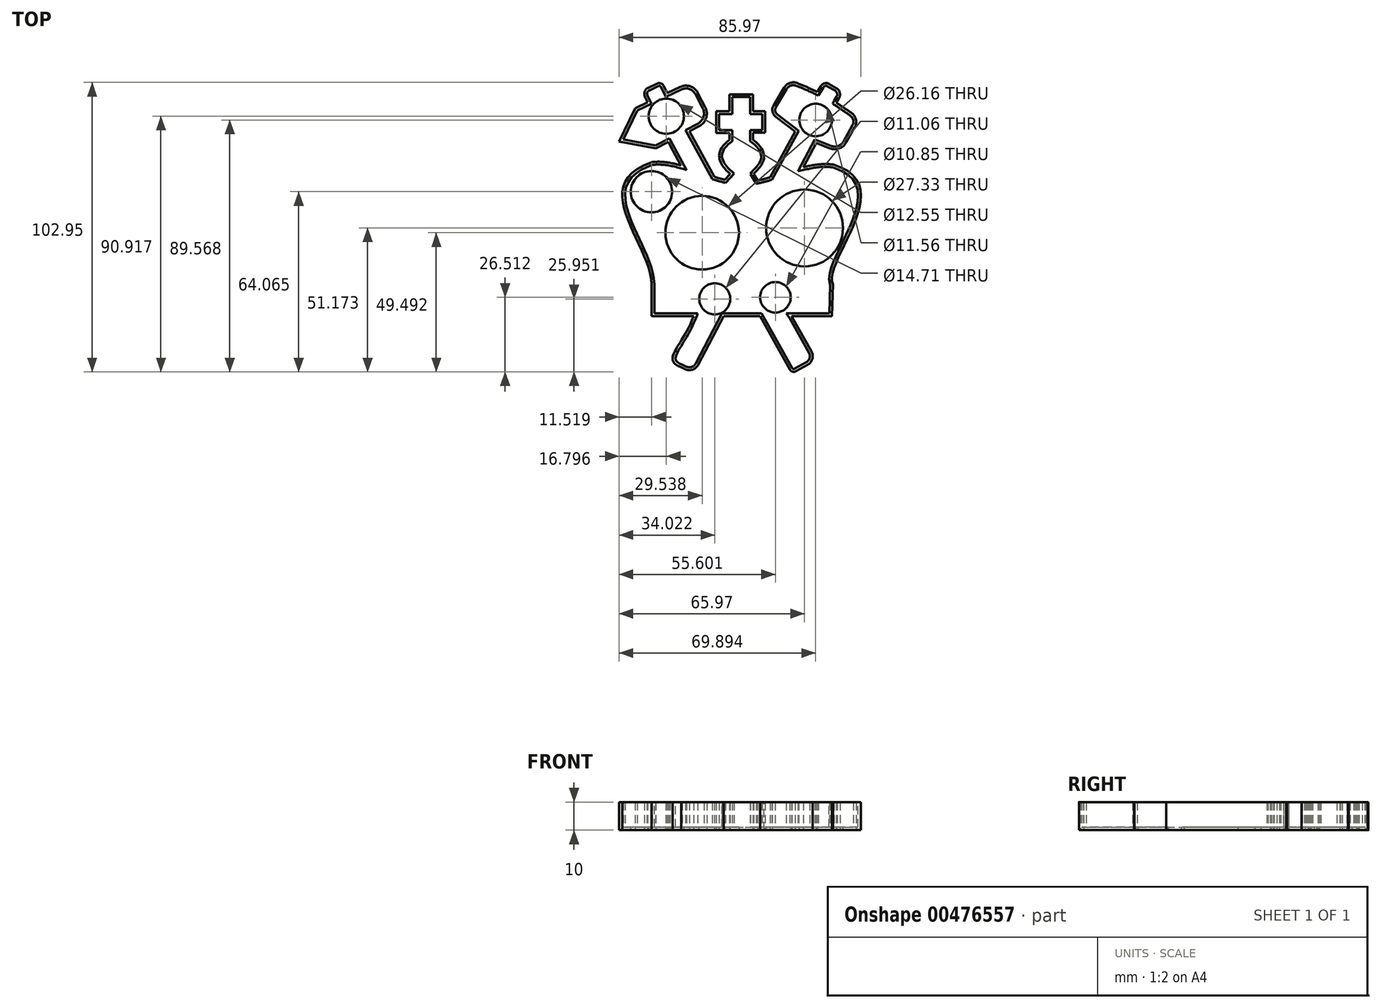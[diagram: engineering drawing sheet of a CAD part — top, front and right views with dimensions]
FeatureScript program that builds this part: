
annotation { "Feature Type Name" : "Feature", "Feature Type Description" : "" }
export const myFeature = defineFeature(function(context is Context, id is Id, definition is map)
    precondition{}
    {
        {
            var Q0;
            Q0=qCreatedBy(makeId("Top.planeOp"),FACE);
            var sketch = newSketch(context, id + "F0", { "sketchPlane" : qUnion([Q0])});
            skLineSegment(sketch, "E0", {"start": v(-31.75, -27.45) * mm, "end": v(32.44, -27.45) * mm});
            skLineSegment(sketch, "E1", {"start": v(-31.75, -27.45) * mm, "end": v(-31.75, -16.16) * mm});
            skLineSegment(sketch, "E2", {"start": v(-31.75, -16.16) * mm, "end": v(32.84, -16.16) * mm});
            skLineSegment(sketch, "E3", {"start": v(32.84, -16.16) * mm, "end": v(32.44, -27.45) * mm});
            skFitSpline(sketch, "E4", {"points": [v(-16.76, -27.45) * mm, v(-21.2, -45.6) * mm], "startDerivative": vector(-12.7, -33.27) * mm, "endDerivative": vector(21.77, -7.86) * mm});
            skLineSegment(sketch, "E5", {"start": v(-21.2, -45.6) * mm, "end": v(-19.95, -46.24) * mm});
            skLineSegment(sketch, "E6", {"start": v(-15.02, -44.65) * mm, "end": v(-6.11, -27.45) * mm});
            skPoint(sketch, "E7.visualSharp", {"position": v(-16.7, -47.89) * mm});
            skArc(sketch, "E7.filletArc", {"start": v(-19.95, -46.24) * mm, "mid": v(-17.16, -46.46) * mm, "end": v(-15.02, -44.65) * mm});
            skLineSegment(sketch, "E8", {"start": v(6.83, -27.45) * mm, "end": v(17.44, -46.43) * mm});
            skLineSegment(sketch, "E9", {"start": v(19.63, -47.05) * mm, "end": v(23.82, -44.7) * mm});
            skLineSegment(sketch, "E10", {"start": v(25.14, -40.03) * mm, "end": v(18.22, -27.65) * mm});
            skPoint(sketch, "E11.visualSharp", {"position": v(18.22, -47.84) * mm});
            skArc(sketch, "E11.filletArc", {"start": v(17.44, -46.43) * mm, "mid": v(18.4, -47.2) * mm, "end": v(19.63, -47.05) * mm});
            skPoint(sketch, "E12.visualSharp", {"position": v(26.82, -43.03) * mm});
            skArc(sketch, "E12.filletArc", {"start": v(23.82, -44.7) * mm, "mid": v(25.45, -42.64) * mm, "end": v(25.14, -40.03) * mm});
            skFitSpline(sketch, "E13", {"points": [v(32.84, -16.16) * mm, v(32.84, 26.48) * mm], "startDerivative": vector(-12.24, 24.57) * mm, "endDerivative": vector(-72.32, 21.35) * mm});
            skFitSpline(sketch, "E14", {"points": [v(-31.75, -16.16) * mm, v(-31.75, 27.32) * mm], "startDerivative": vector(0, 42.93) * mm, "endDerivative": vector(70.07, 24.77) * mm});
            skFitSpline(sketch, "E15", {"points": [v(-31.75, 27.32) * mm, v(-5.7, 21.06) * mm], "startDerivative": vector(25.6, 3.42) * mm, "endDerivative": vector(26.19, -6.26) * mm});
            skFitSpline(sketch, "E16", {"points": [v(32.84, 26.48) * mm, v(5.98, 20.79) * mm], "startDerivative": vector(-26.76, 3.42) * mm, "endDerivative": vector(-26.86, -5.7) * mm});
            skLineSegment(sketch, "E17", {"start": v(-3.75, 23.15) * mm, "end": v(-5.7, 21.06) * mm});
            skLineSegment(sketch, "E18", {"start": v(5.98, 20.79) * mm, "end": v(4.63, 23.15) * mm});
            skFitSpline(sketch, "E19", {"points": [v(-4, 35.28) * mm, v(-3.75, 23.15) * mm], "startDerivative": vector(-23.33, -16.93) * mm, "endDerivative": vector(3.6, -3.25) * mm});
            skFitSpline(sketch, "E20", {"points": [v(4.36, 35.3) * mm, v(4.63, 23.15) * mm], "startDerivative": vector(25.18, -18.88) * mm, "endDerivative": vector(-1.5, -3.03) * mm});
            skLineSegment(sketch, "E21", {"start": v(-4, 35.28) * mm, "end": v(-4, 37.73) * mm});
            skLineSegment(sketch, "E22", {"start": v(-4, 37.73) * mm, "end": v(-8.68, 37.73) * mm});
            skLineSegment(sketch, "E23", {"start": v(-8.68, 37.73) * mm, "end": v(-8.68, 45.48) * mm});
            skLineSegment(sketch, "E24", {"start": v(-8.68, 45.48) * mm, "end": v(-4, 45.48) * mm});
            skLineSegment(sketch, "E25", {"start": v(-4, 45.48) * mm, "end": v(-4, 51.47) * mm});
            skLineSegment(sketch, "E26", {"start": v(-4, 51.47) * mm, "end": v(4.33, 51.47) * mm});
            skLineSegment(sketch, "E27", {"start": v(4.33, 51.47) * mm, "end": v(4.33, 45.48) * mm});
            skLineSegment(sketch, "E28", {"start": v(4.33, 45.48) * mm, "end": v(8.67, 45.48) * mm});
            skLineSegment(sketch, "E29", {"start": v(8.67, 45.48) * mm, "end": v(8.67, 37.77) * mm});
            skLineSegment(sketch, "E30", {"start": v(8.67, 37.77) * mm, "end": v(4.33, 37.77) * mm});
            skLineSegment(sketch, "E31", {"start": v(4.33, 37.77) * mm, "end": v(4.36, 35.3) * mm});
            skLineSegment(sketch, "E32", {"start": v(-25.1, 33.23) * mm, "end": v(-21.27, 26.17) * mm});
            skLineSegment(sketch, "E33", {"start": v(-17.56, 36.97) * mm, "end": v(-9.38, 22.1) * mm});
            skLineSegment(sketch, "E34", {"start": v(-30.16, 32.2) * mm, "end": v(-14.78, 40.15) * mm});
            skLineSegment(sketch, "E35", {"start": v(-12.63, 46.88) * mm, "end": v(-15.27, 51.99) * mm});
            skLineSegment(sketch, "E36", {"start": v(-21.5, 54.09) * mm, "end": v(-37.53, 46.46) * mm});
            skLineSegment(sketch, "E37", {"start": v(-37.53, 46.46) * mm, "end": v(-43.27, 34.66) * mm});
            skLineSegment(sketch, "E38", {"start": v(-43.27, 34.66) * mm, "end": v(-30.16, 32.2) * mm});
            skLineSegment(sketch, "E39", {"start": v(-25.1, 33.23) * mm, "end": v(-25.74, 34.48) * mm});
            skLineSegment(sketch, "E40", {"start": v(-17.56, 36.97) * mm, "end": v(-18.31, 38.32) * mm});
            skLineSegment(sketch, "E41", {"start": v(-33.1, 48.56) * mm, "end": v(-34.08, 50.62) * mm});
            skLineSegment(sketch, "E42", {"start": v(-32.96, 53.76) * mm, "end": v(-29.82, 55.26) * mm});
            skLineSegment(sketch, "E43", {"start": v(-27.37, 54.39) * mm, "end": v(-26.17, 51.86) * mm});
            skPoint(sketch, "E44.visualSharp", {"position": v(-35.1, 52.75) * mm});
            skArc(sketch, "E44.filletArc", {"start": v(-32.96, 53.76) * mm, "mid": v(-34.17, 52.42) * mm, "end": v(-34.08, 50.62) * mm});
            skPoint(sketch, "E45.visualSharp", {"position": v(-28.16, 56.05) * mm});
            skArc(sketch, "E45.filletArc", {"start": v(-27.37, 54.39) * mm, "mid": v(-28.42, 55.33) * mm, "end": v(-29.82, 55.26) * mm});
            skPoint(sketch, "E46.visualSharp", {"position": v(-17.36, 56.05) * mm});
            skArc(sketch, "E46.filletArc", {"start": v(-15.27, 51.99) * mm, "mid": v(-17.96, 54.3) * mm, "end": v(-21.5, 54.09) * mm});
            skPoint(sketch, "E47.visualSharp", {"position": v(-10.33, 42.44) * mm});
            skArc(sketch, "E47.filletArc", {"start": v(-14.78, 40.15) * mm, "mid": v(-12.3, 43.07) * mm, "end": v(-12.63, 46.88) * mm});
            skLineSegment(sketch, "E48", {"start": v(10.45, 21.94) * mm, "end": v(19.31, 38.18) * mm});
            skLineSegment(sketch, "E49", {"start": v(19.31, 38.18) * mm, "end": v(12.43, 43.46) * mm});
            skLineSegment(sketch, "E50", {"start": v(11.66, 47.45) * mm, "end": v(15.45, 53.84) * mm});
            skLineSegment(sketch, "E51", {"start": v(22.3, 25.56) * mm, "end": v(26.79, 34.15) * mm});
            skLineSegment(sketch, "E52", {"start": v(26.79, 34.15) * mm, "end": v(31.71, 32.23) * mm});
            skLineSegment(sketch, "E53", {"start": v(37.54, 34.35) * mm, "end": v(40.6, 39.92) * mm});
            skFitSpline(sketch, "E54", {"points": [v(17.08, 56.6) * mm, v(42.2, 42.82) * mm], "startDerivative": vector(39.32, -14.81) * mm, "endDerivative": vector(25.28, -17.62) * mm});
            skPoint(sketch, "E55.visualSharp", {"position": v(10.28, 45.12) * mm});
            skArc(sketch, "E55.filletArc", {"start": v(11.66, 47.45) * mm, "mid": v(11.29, 45.31) * mm, "end": v(12.43, 43.46) * mm});
            skPoint(sketch, "E56.visualSharp", {"position": v(35.56, 30.73) * mm});
            skArc(sketch, "E56.filletArc", {"start": v(31.71, 32.23) * mm, "mid": v(35.03, 32.2) * mm, "end": v(37.54, 34.35) * mm});
            skArc(sketch, "E57.filletArc", {"start": v(40.6, 39.92) * mm, "mid": v(40.96, 42.53) * mm, "end": v(39.49, 44.72) * mm});
            skArc(sketch, "E58.filletArc", {"start": v(20.12, 55.43) * mm, "mid": v(17.49, 55.5) * mm, "end": v(15.45, 53.84) * mm});
            skLineSegment(sketch, "E59", {"start": v(27.2, 52.32) * mm, "end": v(28.49, 54.4) * mm});
            skLineSegment(sketch, "E60", {"start": v(31.45, 55.14) * mm, "end": v(34.06, 53.62) * mm});
            skLineSegment(sketch, "E61", {"start": v(34.97, 50.17) * mm, "end": v(34.1, 48.7) * mm});
            skPoint(sketch, "E62.visualSharp", {"position": v(29.61, 56.2) * mm});
            skArc(sketch, "E62.filletArc", {"start": v(31.45, 55.14) * mm, "mid": v(29.82, 55.37) * mm, "end": v(28.49, 54.4) * mm});
            skPoint(sketch, "E63.visualSharp", {"position": v(36.24, 52.35) * mm});
            skArc(sketch, "E63.filletArc", {"start": v(34.97, 50.17) * mm, "mid": v(35.23, 52.08) * mm, "end": v(34.06, 53.62) * mm});
            skLineSegment(sketch, "E64", {"start": v(34.1, 48.7) * mm, "end": v(34, 48.47) * mm});
            skLineSegment(sketch, "E65", {"start": v(34, 48.47) * mm, "end": v(34, 48.47) * mm});
            skLineSegment(sketch, "E66", {"start": v(34, 48.47) * mm, "end": v(33.98, 48.44) * mm});
            skLineSegment(sketch, "E67", {"start": v(18.08, -27.45) * mm, "end": v(18.22, -27.65) * mm});
            skCircle(sketch, "E68", {"center": v(-26.47, 43.67) * mm, "radius": 5.28 * mm});
            skCircle(sketch, "E69", {"center": v(26.62, 42.32) * mm, "radius": 4.78 * mm});
            skCircle(sketch, "E70", {"center": v(-13.73, 2.24) * mm, "radius": 13.08 * mm});
            skCircle(sketch, "E71", {"center": v(22.7, 3.92) * mm, "radius": 12.66 * mm});
            skCircle(sketch, "E72", {"center": v(12.33, -20.74) * mm, "radius": 4.42 * mm});
            skCircle(sketch, "E73", {"center": v(-9.25, -21.3) * mm, "radius": 4.53 * mm});
            skPoint(sketch, "E74.centerSnap0", {"position": v(12.13, -36.94) * mm});
            skCircle(sketch, "E75", {"center": v(-31.75, 16.81) * mm, "radius": 6.36 * mm});
            skSolve(sketch);
        }
        {
            var Q0;
            Q0 = qSketchRegion(id + "F0", true);
            extrude(context, id + "F1", {"entities" : qUnion([Q0]), "depth" : 10 * mm});
        }
        {
            var Q0;
            Q0=makeQuery(id+"F1.opExtrude","SWEPT_FACE",FACE,{"disambiguationData":[OSD([sQuery(id+"F0.wireOp",EDGE,"E70")])]});
            var Q1;
            Q1=makeQuery(id+"F1.opExtrude","CAP_FACE",FACE,{"disambiguationData":[OSD([sQuery(id+"F0.wireOp",EDGE,"E0"),sQuery(id+"F0.wireOp",EDGE,"E1"),sQuery(id+"F0.wireOp",EDGE,"E3"),sQuery(id+"F0.wireOp",EDGE,"E4"),sQuery(id+"F0.wireOp",EDGE,"E5"),sQuery(id+"F0.wireOp",EDGE,"E6"),sQuery(id+"F0.wireOp",EDGE,"E7.filletArc"),sQuery(id+"F0.wireOp",EDGE,"E8"),sQuery(id+"F0.wireOp",EDGE,"E9"),sQuery(id+"F0.wireOp",EDGE,"E10"),sQuery(id+"F0.wireOp",EDGE,"E11.filletArc"),sQuery(id+"F0.wireOp",EDGE,"E12.filletArc"),sQuery(id+"F0.wireOp",EDGE,"E13"),sQuery(id+"F0.wireOp",EDGE,"E14"),sQuery(id+"F0.wireOp",EDGE,"E15"),sQuery(id+"F0.wireOp",EDGE,"E16"),sQuery(id+"F0.wireOp",EDGE,"E17"),sQuery(id+"F0.wireOp",EDGE,"E18"),sQuery(id+"F0.wireOp",EDGE,"E19"),sQuery(id+"F0.wireOp",EDGE,"E20"),sQuery(id+"F0.wireOp",EDGE,"E21"),sQuery(id+"F0.wireOp",EDGE,"E22"),sQuery(id+"F0.wireOp",EDGE,"E23"),sQuery(id+"F0.wireOp",EDGE,"E24"),sQuery(id+"F0.wireOp",EDGE,"E25"),sQuery(id+"F0.wireOp",EDGE,"E26"),sQuery(id+"F0.wireOp",EDGE,"E27"),sQuery(id+"F0.wireOp",EDGE,"E28"),sQuery(id+"F0.wireOp",EDGE,"E29"),sQuery(id+"F0.wireOp",EDGE,"E30"),sQuery(id+"F0.wireOp",EDGE,"E31"),sQuery(id+"F0.wireOp",EDGE,"E32"),sQuery(id+"F0.wireOp",EDGE,"E33"),sQuery(id+"F0.wireOp",EDGE,"E34"),sQuery(id+"F0.wireOp",EDGE,"E35"),sQuery(id+"F0.wireOp",EDGE,"E36"),sQuery(id+"F0.wireOp",EDGE,"E37"),sQuery(id+"F0.wireOp",EDGE,"E38"),sQuery(id+"F0.wireOp",EDGE,"E39"),sQuery(id+"F0.wireOp",EDGE,"E40"),sQuery(id+"F0.wireOp",EDGE,"E41"),sQuery(id+"F0.wireOp",EDGE,"E42"),sQuery(id+"F0.wireOp",EDGE,"E43"),sQuery(id+"F0.wireOp",EDGE,"E44.filletArc"),sQuery(id+"F0.wireOp",EDGE,"E45.filletArc"),sQuery(id+"F0.wireOp",EDGE,"E46.filletArc"),sQuery(id+"F0.wireOp",EDGE,"E47.filletArc"),sQuery(id+"F0.wireOp",EDGE,"E48"),sQuery(id+"F0.wireOp",EDGE,"E49"),sQuery(id+"F0.wireOp",EDGE,"E50"),sQuery(id+"F0.wireOp",EDGE,"E51"),sQuery(id+"F0.wireOp",EDGE,"E52"),sQuery(id+"F0.wireOp",EDGE,"E53"),sQuery(id+"F0.wireOp",EDGE,"E54"),sQuery(id+"F0.wireOp",EDGE,"E55.filletArc"),sQuery(id+"F0.wireOp",EDGE,"E56.filletArc"),sQuery(id+"F0.wireOp",EDGE,"E57.filletArc"),sQuery(id+"F0.wireOp",EDGE,"E58.filletArc"),sQuery(id+"F0.wireOp",EDGE,"E59"),sQuery(id+"F0.wireOp",EDGE,"E60"),sQuery(id+"F0.wireOp",EDGE,"E61"),sQuery(id+"F0.wireOp",EDGE,"E62.filletArc"),sQuery(id+"F0.wireOp",EDGE,"E63.filletArc"),sQuery(id+"F0.wireOp",EDGE,"E64"),sQuery(id+"F0.wireOp",EDGE,"E67"),sQuery(id+"F0.wireOp",EDGE,"E68"),sQuery(id+"F0.wireOp",EDGE,"E69"),sQuery(id+"F0.wireOp",EDGE,"E70"),sQuery(id+"F0.wireOp",EDGE,"E71"),sQuery(id+"F0.wireOp",EDGE,"E72"),sQuery(id+"F0.wireOp",EDGE,"E73"),sQuery(id+"F0.wireOp",EDGE,"E75")])],"isStart":false});
            shell(context, id + "F2", {"entities" : qUnion([Q0, Q1]), "thickness" : 1 * mm});
        }
        {
            var Q0;
            {var subQ0=sQuery(id+"F0.wireOp",EDGE,"E75");var subQ1=sQuery(id+"F0.wireOp",EDGE,"E73");var subQ2=sQuery(id+"F0.wireOp",EDGE,"E72");var subQ3=sQuery(id+"F0.wireOp",EDGE,"E71");var subQ4=sQuery(id+"F0.wireOp",EDGE,"E70");var subQ5=sQuery(id+"F0.wireOp",EDGE,"E69");var subQ6=sQuery(id+"F0.wireOp",EDGE,"E68");var subQ7=sQuery(id+"F0.wireOp",EDGE,"E67");var subQ8=sQuery(id+"F0.wireOp",EDGE,"E64");var subQ9=sQuery(id+"F0.wireOp",EDGE,"E63.filletArc");var subQ10=sQuery(id+"F0.wireOp",EDGE,"E62.filletArc");var subQ11=sQuery(id+"F0.wireOp",EDGE,"E61");var subQ12=sQuery(id+"F0.wireOp",EDGE,"E60");var subQ13=sQuery(id+"F0.wireOp",EDGE,"E59");var subQ14=sQuery(id+"F0.wireOp",EDGE,"E58.filletArc");var subQ15=sQuery(id+"F0.wireOp",EDGE,"E57.filletArc");var subQ16=sQuery(id+"F0.wireOp",EDGE,"E56.filletArc");var subQ17=sQuery(id+"F0.wireOp",EDGE,"E55.filletArc");var subQ18=sQuery(id+"F0.wireOp",EDGE,"E54");var subQ19=sQuery(id+"F0.wireOp",EDGE,"E53");var subQ20=sQuery(id+"F0.wireOp",EDGE,"E52");var subQ21=sQuery(id+"F0.wireOp",EDGE,"E51");var subQ22=sQuery(id+"F0.wireOp",EDGE,"E50");var subQ23=sQuery(id+"F0.wireOp",EDGE,"E49");var subQ24=sQuery(id+"F0.wireOp",EDGE,"E48");var subQ25=sQuery(id+"F0.wireOp",EDGE,"E47.filletArc");var subQ26=sQuery(id+"F0.wireOp",EDGE,"E46.filletArc");var subQ27=sQuery(id+"F0.wireOp",EDGE,"E45.filletArc");var subQ28=sQuery(id+"F0.wireOp",EDGE,"E44.filletArc");var subQ29=sQuery(id+"F0.wireOp",EDGE,"E43");var subQ30=sQuery(id+"F0.wireOp",EDGE,"E42");var subQ31=sQuery(id+"F0.wireOp",EDGE,"E41");var subQ32=sQuery(id+"F0.wireOp",EDGE,"E40");var subQ33=sQuery(id+"F0.wireOp",EDGE,"E39");var subQ34=sQuery(id+"F0.wireOp",EDGE,"E38");var subQ35=sQuery(id+"F0.wireOp",EDGE,"E37");var subQ36=sQuery(id+"F0.wireOp",EDGE,"E36");var subQ37=sQuery(id+"F0.wireOp",EDGE,"E35");var subQ38=sQuery(id+"F0.wireOp",EDGE,"E34");var subQ39=sQuery(id+"F0.wireOp",EDGE,"E33");var subQ40=sQuery(id+"F0.wireOp",EDGE,"E32");var subQ41=sQuery(id+"F0.wireOp",EDGE,"E31");var subQ42=sQuery(id+"F0.wireOp",EDGE,"E30");var subQ43=sQuery(id+"F0.wireOp",EDGE,"E29");var subQ44=sQuery(id+"F0.wireOp",EDGE,"E28");var subQ45=sQuery(id+"F0.wireOp",EDGE,"E27");var subQ46=sQuery(id+"F0.wireOp",EDGE,"E26");var subQ47=sQuery(id+"F0.wireOp",EDGE,"E25");var subQ48=sQuery(id+"F0.wireOp",EDGE,"E24");var subQ49=sQuery(id+"F0.wireOp",EDGE,"E23");var subQ50=sQuery(id+"F0.wireOp",EDGE,"E22");var subQ51=sQuery(id+"F0.wireOp",EDGE,"E21");var subQ52=sQuery(id+"F0.wireOp",EDGE,"E20");var subQ53=sQuery(id+"F0.wireOp",EDGE,"E19");var subQ54=sQuery(id+"F0.wireOp",EDGE,"E18");var subQ55=sQuery(id+"F0.wireOp",EDGE,"E17");var subQ56=sQuery(id+"F0.wireOp",EDGE,"E16");var subQ57=sQuery(id+"F0.wireOp",EDGE,"E15");var subQ58=sQuery(id+"F0.wireOp",EDGE,"E14");var subQ59=sQuery(id+"F0.wireOp",EDGE,"E13");var subQ60=sQuery(id+"F0.wireOp",EDGE,"E12.filletArc");var subQ61=sQuery(id+"F0.wireOp",EDGE,"E11.filletArc");var subQ62=sQuery(id+"F0.wireOp",EDGE,"E10");var subQ63=sQuery(id+"F0.wireOp",EDGE,"E9");var subQ64=sQuery(id+"F0.wireOp",EDGE,"E8");var subQ65=sQuery(id+"F0.wireOp",EDGE,"E7.filletArc");var subQ66=sQuery(id+"F0.wireOp",EDGE,"E6");var subQ67=sQuery(id+"F0.wireOp",EDGE,"E5");var subQ68=sQuery(id+"F0.wireOp",EDGE,"E4");var subQ69=sQuery(id+"F0.wireOp",EDGE,"E3");var subQ70=sQuery(id+"F0.wireOp",EDGE,"E1");var subQ71=sQuery(id+"F0.wireOp",EDGE,"E0");Q0=makeQuery(id+"F2.opShell","OFFSET_FACE",FACE,{"disambiguationData":[OSD([subQ71,subQ70,subQ69,subQ68,subQ67,subQ66,subQ65,subQ64,subQ63,subQ62,subQ61,subQ60,subQ59,subQ58,subQ57,subQ56,subQ55,subQ54,subQ53,subQ52,subQ51,subQ50,subQ49,subQ48,subQ47,subQ46,subQ45,subQ44,subQ43,subQ42,subQ41,subQ40,subQ39,subQ38,subQ37,subQ36,subQ35,subQ34,subQ33,subQ32,subQ31,subQ30,subQ29,subQ28,subQ27,subQ26,subQ25,subQ24,subQ23,subQ22,subQ21,subQ20,subQ19,subQ18,subQ17,subQ16,subQ15,subQ14,subQ13,subQ12,subQ11,subQ10,subQ9,subQ8,subQ7,subQ6,subQ5,subQ4,subQ3,subQ2,subQ1,subQ0]),TDD([makeQuery(id+"F1.opExtrude","CAP_FACE",FACE,{"disambiguationData":[OSD([subQ71,subQ70,subQ69,subQ68,subQ67,subQ66,subQ65,subQ64,subQ63,subQ62,subQ61,subQ60,subQ59,subQ58,subQ57,subQ56,subQ55,subQ54,subQ53,subQ52,subQ51,subQ50,subQ49,subQ48,subQ47,subQ46,subQ45,subQ44,subQ43,subQ42,subQ41,subQ40,subQ39,subQ38,subQ37,subQ36,subQ35,subQ34,subQ33,subQ32,subQ31,subQ30,subQ29,subQ28,subQ27,subQ26,subQ25,subQ24,subQ23,subQ22,subQ21,subQ20,subQ19,subQ18,subQ17,subQ16,subQ15,subQ14,subQ13,subQ12,subQ11,subQ10,subQ9,subQ8,subQ7,subQ6,subQ5,subQ4,subQ3,subQ2,subQ1,subQ0])],"isStart":false})]),OD(4.0)]});}
            extrude(context, id + "F3", {"entities" : qUnion([Q0]), "operationType" : NewBodyOperationType.REMOVE, "oppositeDirection" : true, "depth" : 25 * mm});
        }
        {
            var Q0;
            {var subQ0=sQuery(id+"F0.wireOp",EDGE,"E75");var subQ1=sQuery(id+"F0.wireOp",EDGE,"E73");var subQ2=sQuery(id+"F0.wireOp",EDGE,"E72");var subQ3=sQuery(id+"F0.wireOp",EDGE,"E71");var subQ4=sQuery(id+"F0.wireOp",EDGE,"E70");var subQ5=sQuery(id+"F0.wireOp",EDGE,"E69");var subQ6=sQuery(id+"F0.wireOp",EDGE,"E68");var subQ7=sQuery(id+"F0.wireOp",EDGE,"E67");var subQ8=sQuery(id+"F0.wireOp",EDGE,"E64");var subQ9=sQuery(id+"F0.wireOp",EDGE,"E63.filletArc");var subQ10=sQuery(id+"F0.wireOp",EDGE,"E62.filletArc");var subQ11=sQuery(id+"F0.wireOp",EDGE,"E61");var subQ12=sQuery(id+"F0.wireOp",EDGE,"E60");var subQ13=sQuery(id+"F0.wireOp",EDGE,"E59");var subQ14=sQuery(id+"F0.wireOp",EDGE,"E58.filletArc");var subQ15=sQuery(id+"F0.wireOp",EDGE,"E57.filletArc");var subQ16=sQuery(id+"F0.wireOp",EDGE,"E56.filletArc");var subQ17=sQuery(id+"F0.wireOp",EDGE,"E55.filletArc");var subQ18=sQuery(id+"F0.wireOp",EDGE,"E54");var subQ19=sQuery(id+"F0.wireOp",EDGE,"E53");var subQ20=sQuery(id+"F0.wireOp",EDGE,"E52");var subQ21=sQuery(id+"F0.wireOp",EDGE,"E51");var subQ22=sQuery(id+"F0.wireOp",EDGE,"E50");var subQ23=sQuery(id+"F0.wireOp",EDGE,"E49");var subQ24=sQuery(id+"F0.wireOp",EDGE,"E48");var subQ25=sQuery(id+"F0.wireOp",EDGE,"E47.filletArc");var subQ26=sQuery(id+"F0.wireOp",EDGE,"E46.filletArc");var subQ27=sQuery(id+"F0.wireOp",EDGE,"E45.filletArc");var subQ28=sQuery(id+"F0.wireOp",EDGE,"E44.filletArc");var subQ29=sQuery(id+"F0.wireOp",EDGE,"E43");var subQ30=sQuery(id+"F0.wireOp",EDGE,"E42");var subQ31=sQuery(id+"F0.wireOp",EDGE,"E41");var subQ32=sQuery(id+"F0.wireOp",EDGE,"E40");var subQ33=sQuery(id+"F0.wireOp",EDGE,"E39");var subQ34=sQuery(id+"F0.wireOp",EDGE,"E38");var subQ35=sQuery(id+"F0.wireOp",EDGE,"E37");var subQ36=sQuery(id+"F0.wireOp",EDGE,"E36");var subQ37=sQuery(id+"F0.wireOp",EDGE,"E35");var subQ38=sQuery(id+"F0.wireOp",EDGE,"E34");var subQ39=sQuery(id+"F0.wireOp",EDGE,"E33");var subQ40=sQuery(id+"F0.wireOp",EDGE,"E32");var subQ41=sQuery(id+"F0.wireOp",EDGE,"E31");var subQ42=sQuery(id+"F0.wireOp",EDGE,"E30");var subQ43=sQuery(id+"F0.wireOp",EDGE,"E29");var subQ44=sQuery(id+"F0.wireOp",EDGE,"E28");var subQ45=sQuery(id+"F0.wireOp",EDGE,"E27");var subQ46=sQuery(id+"F0.wireOp",EDGE,"E26");var subQ47=sQuery(id+"F0.wireOp",EDGE,"E25");var subQ48=sQuery(id+"F0.wireOp",EDGE,"E24");var subQ49=sQuery(id+"F0.wireOp",EDGE,"E23");var subQ50=sQuery(id+"F0.wireOp",EDGE,"E22");var subQ51=sQuery(id+"F0.wireOp",EDGE,"E21");var subQ52=sQuery(id+"F0.wireOp",EDGE,"E20");var subQ53=sQuery(id+"F0.wireOp",EDGE,"E19");var subQ54=sQuery(id+"F0.wireOp",EDGE,"E18");var subQ55=sQuery(id+"F0.wireOp",EDGE,"E17");var subQ56=sQuery(id+"F0.wireOp",EDGE,"E16");var subQ57=sQuery(id+"F0.wireOp",EDGE,"E15");var subQ58=sQuery(id+"F0.wireOp",EDGE,"E14");var subQ59=sQuery(id+"F0.wireOp",EDGE,"E13");var subQ60=sQuery(id+"F0.wireOp",EDGE,"E12.filletArc");var subQ61=sQuery(id+"F0.wireOp",EDGE,"E11.filletArc");var subQ62=sQuery(id+"F0.wireOp",EDGE,"E10");var subQ63=sQuery(id+"F0.wireOp",EDGE,"E9");var subQ64=sQuery(id+"F0.wireOp",EDGE,"E8");var subQ65=sQuery(id+"F0.wireOp",EDGE,"E7.filletArc");var subQ66=sQuery(id+"F0.wireOp",EDGE,"E6");var subQ67=sQuery(id+"F0.wireOp",EDGE,"E5");var subQ68=sQuery(id+"F0.wireOp",EDGE,"E4");var subQ69=sQuery(id+"F0.wireOp",EDGE,"E3");var subQ70=sQuery(id+"F0.wireOp",EDGE,"E1");var subQ71=sQuery(id+"F0.wireOp",EDGE,"E0");Q0=makeQuery(id+"F2.opShell","OFFSET_FACE",FACE,{"disambiguationData":[OSD([subQ71,subQ70,subQ69,subQ68,subQ67,subQ66,subQ65,subQ64,subQ63,subQ62,subQ61,subQ60,subQ59,subQ58,subQ57,subQ56,subQ55,subQ54,subQ53,subQ52,subQ51,subQ50,subQ49,subQ48,subQ47,subQ46,subQ45,subQ44,subQ43,subQ42,subQ41,subQ40,subQ39,subQ38,subQ37,subQ36,subQ35,subQ34,subQ33,subQ32,subQ31,subQ30,subQ29,subQ28,subQ27,subQ26,subQ25,subQ24,subQ23,subQ22,subQ21,subQ20,subQ19,subQ18,subQ17,subQ16,subQ15,subQ14,subQ13,subQ12,subQ11,subQ10,subQ9,subQ8,subQ7,subQ6,subQ5,subQ4,subQ3,subQ2,subQ1,subQ0]),TDD([makeQuery(id+"F1.opExtrude","CAP_FACE",FACE,{"disambiguationData":[OSD([subQ71,subQ70,subQ69,subQ68,subQ67,subQ66,subQ65,subQ64,subQ63,subQ62,subQ61,subQ60,subQ59,subQ58,subQ57,subQ56,subQ55,subQ54,subQ53,subQ52,subQ51,subQ50,subQ49,subQ48,subQ47,subQ46,subQ45,subQ44,subQ43,subQ42,subQ41,subQ40,subQ39,subQ38,subQ37,subQ36,subQ35,subQ34,subQ33,subQ32,subQ31,subQ30,subQ29,subQ28,subQ27,subQ26,subQ25,subQ24,subQ23,subQ22,subQ21,subQ20,subQ19,subQ18,subQ17,subQ16,subQ15,subQ14,subQ13,subQ12,subQ11,subQ10,subQ9,subQ8,subQ7,subQ6,subQ5,subQ4,subQ3,subQ2,subQ1,subQ0])],"isStart":false})]),OD(0.0)]});}
            var Q1;
            {var subQ0=sQuery(id+"F0.wireOp",EDGE,"E75");var subQ1=sQuery(id+"F0.wireOp",EDGE,"E73");var subQ2=sQuery(id+"F0.wireOp",EDGE,"E72");var subQ3=sQuery(id+"F0.wireOp",EDGE,"E71");var subQ4=sQuery(id+"F0.wireOp",EDGE,"E70");var subQ5=sQuery(id+"F0.wireOp",EDGE,"E69");var subQ6=sQuery(id+"F0.wireOp",EDGE,"E68");var subQ7=sQuery(id+"F0.wireOp",EDGE,"E67");var subQ8=sQuery(id+"F0.wireOp",EDGE,"E64");var subQ9=sQuery(id+"F0.wireOp",EDGE,"E63.filletArc");var subQ10=sQuery(id+"F0.wireOp",EDGE,"E62.filletArc");var subQ11=sQuery(id+"F0.wireOp",EDGE,"E61");var subQ12=sQuery(id+"F0.wireOp",EDGE,"E60");var subQ13=sQuery(id+"F0.wireOp",EDGE,"E59");var subQ14=sQuery(id+"F0.wireOp",EDGE,"E58.filletArc");var subQ15=sQuery(id+"F0.wireOp",EDGE,"E57.filletArc");var subQ16=sQuery(id+"F0.wireOp",EDGE,"E56.filletArc");var subQ17=sQuery(id+"F0.wireOp",EDGE,"E55.filletArc");var subQ18=sQuery(id+"F0.wireOp",EDGE,"E54");var subQ19=sQuery(id+"F0.wireOp",EDGE,"E53");var subQ20=sQuery(id+"F0.wireOp",EDGE,"E52");var subQ21=sQuery(id+"F0.wireOp",EDGE,"E51");var subQ22=sQuery(id+"F0.wireOp",EDGE,"E50");var subQ23=sQuery(id+"F0.wireOp",EDGE,"E49");var subQ24=sQuery(id+"F0.wireOp",EDGE,"E48");var subQ25=sQuery(id+"F0.wireOp",EDGE,"E47.filletArc");var subQ26=sQuery(id+"F0.wireOp",EDGE,"E46.filletArc");var subQ27=sQuery(id+"F0.wireOp",EDGE,"E45.filletArc");var subQ28=sQuery(id+"F0.wireOp",EDGE,"E44.filletArc");var subQ29=sQuery(id+"F0.wireOp",EDGE,"E43");var subQ30=sQuery(id+"F0.wireOp",EDGE,"E42");var subQ31=sQuery(id+"F0.wireOp",EDGE,"E41");var subQ32=sQuery(id+"F0.wireOp",EDGE,"E40");var subQ33=sQuery(id+"F0.wireOp",EDGE,"E39");var subQ34=sQuery(id+"F0.wireOp",EDGE,"E38");var subQ35=sQuery(id+"F0.wireOp",EDGE,"E37");var subQ36=sQuery(id+"F0.wireOp",EDGE,"E36");var subQ37=sQuery(id+"F0.wireOp",EDGE,"E35");var subQ38=sQuery(id+"F0.wireOp",EDGE,"E34");var subQ39=sQuery(id+"F0.wireOp",EDGE,"E33");var subQ40=sQuery(id+"F0.wireOp",EDGE,"E32");var subQ41=sQuery(id+"F0.wireOp",EDGE,"E31");var subQ42=sQuery(id+"F0.wireOp",EDGE,"E30");var subQ43=sQuery(id+"F0.wireOp",EDGE,"E29");var subQ44=sQuery(id+"F0.wireOp",EDGE,"E28");var subQ45=sQuery(id+"F0.wireOp",EDGE,"E27");var subQ46=sQuery(id+"F0.wireOp",EDGE,"E26");var subQ47=sQuery(id+"F0.wireOp",EDGE,"E25");var subQ48=sQuery(id+"F0.wireOp",EDGE,"E24");var subQ49=sQuery(id+"F0.wireOp",EDGE,"E23");var subQ50=sQuery(id+"F0.wireOp",EDGE,"E22");var subQ51=sQuery(id+"F0.wireOp",EDGE,"E21");var subQ52=sQuery(id+"F0.wireOp",EDGE,"E20");var subQ53=sQuery(id+"F0.wireOp",EDGE,"E19");var subQ54=sQuery(id+"F0.wireOp",EDGE,"E18");var subQ55=sQuery(id+"F0.wireOp",EDGE,"E17");var subQ56=sQuery(id+"F0.wireOp",EDGE,"E16");var subQ57=sQuery(id+"F0.wireOp",EDGE,"E15");var subQ58=sQuery(id+"F0.wireOp",EDGE,"E14");var subQ59=sQuery(id+"F0.wireOp",EDGE,"E13");var subQ60=sQuery(id+"F0.wireOp",EDGE,"E12.filletArc");var subQ61=sQuery(id+"F0.wireOp",EDGE,"E11.filletArc");var subQ62=sQuery(id+"F0.wireOp",EDGE,"E10");var subQ63=sQuery(id+"F0.wireOp",EDGE,"E9");var subQ64=sQuery(id+"F0.wireOp",EDGE,"E8");var subQ65=sQuery(id+"F0.wireOp",EDGE,"E7.filletArc");var subQ66=sQuery(id+"F0.wireOp",EDGE,"E6");var subQ67=sQuery(id+"F0.wireOp",EDGE,"E5");var subQ68=sQuery(id+"F0.wireOp",EDGE,"E4");var subQ69=sQuery(id+"F0.wireOp",EDGE,"E3");var subQ70=sQuery(id+"F0.wireOp",EDGE,"E1");var subQ71=sQuery(id+"F0.wireOp",EDGE,"E0");Q1=makeQuery(id+"F2.opShell","OFFSET_FACE",FACE,{"disambiguationData":[OSD([subQ71,subQ70,subQ69,subQ68,subQ67,subQ66,subQ65,subQ64,subQ63,subQ62,subQ61,subQ60,subQ59,subQ58,subQ57,subQ56,subQ55,subQ54,subQ53,subQ52,subQ51,subQ50,subQ49,subQ48,subQ47,subQ46,subQ45,subQ44,subQ43,subQ42,subQ41,subQ40,subQ39,subQ38,subQ37,subQ36,subQ35,subQ34,subQ33,subQ32,subQ31,subQ30,subQ29,subQ28,subQ27,subQ26,subQ25,subQ24,subQ23,subQ22,subQ21,subQ20,subQ19,subQ18,subQ17,subQ16,subQ15,subQ14,subQ13,subQ12,subQ11,subQ10,subQ9,subQ8,subQ7,subQ6,subQ5,subQ4,subQ3,subQ2,subQ1,subQ0]),TDD([makeQuery(id+"F1.opExtrude","CAP_FACE",FACE,{"disambiguationData":[OSD([subQ71,subQ70,subQ69,subQ68,subQ67,subQ66,subQ65,subQ64,subQ63,subQ62,subQ61,subQ60,subQ59,subQ58,subQ57,subQ56,subQ55,subQ54,subQ53,subQ52,subQ51,subQ50,subQ49,subQ48,subQ47,subQ46,subQ45,subQ44,subQ43,subQ42,subQ41,subQ40,subQ39,subQ38,subQ37,subQ36,subQ35,subQ34,subQ33,subQ32,subQ31,subQ30,subQ29,subQ28,subQ27,subQ26,subQ25,subQ24,subQ23,subQ22,subQ21,subQ20,subQ19,subQ18,subQ17,subQ16,subQ15,subQ14,subQ13,subQ12,subQ11,subQ10,subQ9,subQ8,subQ7,subQ6,subQ5,subQ4,subQ3,subQ2,subQ1,subQ0])],"isStart":false})]),OD(2.0)]});}
            var Q2;
            {var subQ0=sQuery(id+"F0.wireOp",EDGE,"E75");var subQ1=sQuery(id+"F0.wireOp",EDGE,"E73");var subQ2=sQuery(id+"F0.wireOp",EDGE,"E72");var subQ3=sQuery(id+"F0.wireOp",EDGE,"E71");var subQ4=sQuery(id+"F0.wireOp",EDGE,"E70");var subQ5=sQuery(id+"F0.wireOp",EDGE,"E69");var subQ6=sQuery(id+"F0.wireOp",EDGE,"E68");var subQ7=sQuery(id+"F0.wireOp",EDGE,"E67");var subQ8=sQuery(id+"F0.wireOp",EDGE,"E64");var subQ9=sQuery(id+"F0.wireOp",EDGE,"E63.filletArc");var subQ10=sQuery(id+"F0.wireOp",EDGE,"E62.filletArc");var subQ11=sQuery(id+"F0.wireOp",EDGE,"E61");var subQ12=sQuery(id+"F0.wireOp",EDGE,"E60");var subQ13=sQuery(id+"F0.wireOp",EDGE,"E59");var subQ14=sQuery(id+"F0.wireOp",EDGE,"E58.filletArc");var subQ15=sQuery(id+"F0.wireOp",EDGE,"E57.filletArc");var subQ16=sQuery(id+"F0.wireOp",EDGE,"E56.filletArc");var subQ17=sQuery(id+"F0.wireOp",EDGE,"E55.filletArc");var subQ18=sQuery(id+"F0.wireOp",EDGE,"E54");var subQ19=sQuery(id+"F0.wireOp",EDGE,"E53");var subQ20=sQuery(id+"F0.wireOp",EDGE,"E52");var subQ21=sQuery(id+"F0.wireOp",EDGE,"E51");var subQ22=sQuery(id+"F0.wireOp",EDGE,"E50");var subQ23=sQuery(id+"F0.wireOp",EDGE,"E49");var subQ24=sQuery(id+"F0.wireOp",EDGE,"E48");var subQ25=sQuery(id+"F0.wireOp",EDGE,"E47.filletArc");var subQ26=sQuery(id+"F0.wireOp",EDGE,"E46.filletArc");var subQ27=sQuery(id+"F0.wireOp",EDGE,"E45.filletArc");var subQ28=sQuery(id+"F0.wireOp",EDGE,"E44.filletArc");var subQ29=sQuery(id+"F0.wireOp",EDGE,"E43");var subQ30=sQuery(id+"F0.wireOp",EDGE,"E42");var subQ31=sQuery(id+"F0.wireOp",EDGE,"E41");var subQ32=sQuery(id+"F0.wireOp",EDGE,"E40");var subQ33=sQuery(id+"F0.wireOp",EDGE,"E39");var subQ34=sQuery(id+"F0.wireOp",EDGE,"E38");var subQ35=sQuery(id+"F0.wireOp",EDGE,"E37");var subQ36=sQuery(id+"F0.wireOp",EDGE,"E36");var subQ37=sQuery(id+"F0.wireOp",EDGE,"E35");var subQ38=sQuery(id+"F0.wireOp",EDGE,"E34");var subQ39=sQuery(id+"F0.wireOp",EDGE,"E33");var subQ40=sQuery(id+"F0.wireOp",EDGE,"E32");var subQ41=sQuery(id+"F0.wireOp",EDGE,"E31");var subQ42=sQuery(id+"F0.wireOp",EDGE,"E30");var subQ43=sQuery(id+"F0.wireOp",EDGE,"E29");var subQ44=sQuery(id+"F0.wireOp",EDGE,"E28");var subQ45=sQuery(id+"F0.wireOp",EDGE,"E27");var subQ46=sQuery(id+"F0.wireOp",EDGE,"E26");var subQ47=sQuery(id+"F0.wireOp",EDGE,"E25");var subQ48=sQuery(id+"F0.wireOp",EDGE,"E24");var subQ49=sQuery(id+"F0.wireOp",EDGE,"E23");var subQ50=sQuery(id+"F0.wireOp",EDGE,"E22");var subQ51=sQuery(id+"F0.wireOp",EDGE,"E21");var subQ52=sQuery(id+"F0.wireOp",EDGE,"E20");var subQ53=sQuery(id+"F0.wireOp",EDGE,"E19");var subQ54=sQuery(id+"F0.wireOp",EDGE,"E18");var subQ55=sQuery(id+"F0.wireOp",EDGE,"E17");var subQ56=sQuery(id+"F0.wireOp",EDGE,"E16");var subQ57=sQuery(id+"F0.wireOp",EDGE,"E15");var subQ58=sQuery(id+"F0.wireOp",EDGE,"E14");var subQ59=sQuery(id+"F0.wireOp",EDGE,"E13");var subQ60=sQuery(id+"F0.wireOp",EDGE,"E12.filletArc");var subQ61=sQuery(id+"F0.wireOp",EDGE,"E11.filletArc");var subQ62=sQuery(id+"F0.wireOp",EDGE,"E10");var subQ63=sQuery(id+"F0.wireOp",EDGE,"E9");var subQ64=sQuery(id+"F0.wireOp",EDGE,"E8");var subQ65=sQuery(id+"F0.wireOp",EDGE,"E7.filletArc");var subQ66=sQuery(id+"F0.wireOp",EDGE,"E6");var subQ67=sQuery(id+"F0.wireOp",EDGE,"E5");var subQ68=sQuery(id+"F0.wireOp",EDGE,"E4");var subQ69=sQuery(id+"F0.wireOp",EDGE,"E3");var subQ70=sQuery(id+"F0.wireOp",EDGE,"E1");var subQ71=sQuery(id+"F0.wireOp",EDGE,"E0");Q2=makeQuery(id+"F2.opShell","OFFSET_FACE",FACE,{"disambiguationData":[OSD([subQ71,subQ70,subQ69,subQ68,subQ67,subQ66,subQ65,subQ64,subQ63,subQ62,subQ61,subQ60,subQ59,subQ58,subQ57,subQ56,subQ55,subQ54,subQ53,subQ52,subQ51,subQ50,subQ49,subQ48,subQ47,subQ46,subQ45,subQ44,subQ43,subQ42,subQ41,subQ40,subQ39,subQ38,subQ37,subQ36,subQ35,subQ34,subQ33,subQ32,subQ31,subQ30,subQ29,subQ28,subQ27,subQ26,subQ25,subQ24,subQ23,subQ22,subQ21,subQ20,subQ19,subQ18,subQ17,subQ16,subQ15,subQ14,subQ13,subQ12,subQ11,subQ10,subQ9,subQ8,subQ7,subQ6,subQ5,subQ4,subQ3,subQ2,subQ1,subQ0]),TDD([makeQuery(id+"F1.opExtrude","CAP_FACE",FACE,{"disambiguationData":[OSD([subQ71,subQ70,subQ69,subQ68,subQ67,subQ66,subQ65,subQ64,subQ63,subQ62,subQ61,subQ60,subQ59,subQ58,subQ57,subQ56,subQ55,subQ54,subQ53,subQ52,subQ51,subQ50,subQ49,subQ48,subQ47,subQ46,subQ45,subQ44,subQ43,subQ42,subQ41,subQ40,subQ39,subQ38,subQ37,subQ36,subQ35,subQ34,subQ33,subQ32,subQ31,subQ30,subQ29,subQ28,subQ27,subQ26,subQ25,subQ24,subQ23,subQ22,subQ21,subQ20,subQ19,subQ18,subQ17,subQ16,subQ15,subQ14,subQ13,subQ12,subQ11,subQ10,subQ9,subQ8,subQ7,subQ6,subQ5,subQ4,subQ3,subQ2,subQ1,subQ0])],"isStart":false})]),OD(3.0)]});}
            extrude(context, id + "F4", {"entities" : qUnion([Q0, Q1, Q2]), "operationType" : NewBodyOperationType.REMOVE, "oppositeDirection" : true, "depth" : 25 * mm});
        }
        {
            var Q0;
            {var subQ0=sQuery(id+"F0.wireOp",EDGE,"E75");var subQ1=sQuery(id+"F0.wireOp",EDGE,"E73");var subQ2=sQuery(id+"F0.wireOp",EDGE,"E72");var subQ3=sQuery(id+"F0.wireOp",EDGE,"E71");var subQ4=sQuery(id+"F0.wireOp",EDGE,"E70");var subQ5=sQuery(id+"F0.wireOp",EDGE,"E69");var subQ6=sQuery(id+"F0.wireOp",EDGE,"E68");var subQ7=sQuery(id+"F0.wireOp",EDGE,"E67");var subQ8=sQuery(id+"F0.wireOp",EDGE,"E64");var subQ9=sQuery(id+"F0.wireOp",EDGE,"E63.filletArc");var subQ10=sQuery(id+"F0.wireOp",EDGE,"E62.filletArc");var subQ11=sQuery(id+"F0.wireOp",EDGE,"E61");var subQ12=sQuery(id+"F0.wireOp",EDGE,"E60");var subQ13=sQuery(id+"F0.wireOp",EDGE,"E59");var subQ14=sQuery(id+"F0.wireOp",EDGE,"E58.filletArc");var subQ15=sQuery(id+"F0.wireOp",EDGE,"E57.filletArc");var subQ16=sQuery(id+"F0.wireOp",EDGE,"E56.filletArc");var subQ17=sQuery(id+"F0.wireOp",EDGE,"E55.filletArc");var subQ18=sQuery(id+"F0.wireOp",EDGE,"E54");var subQ19=sQuery(id+"F0.wireOp",EDGE,"E53");var subQ20=sQuery(id+"F0.wireOp",EDGE,"E52");var subQ21=sQuery(id+"F0.wireOp",EDGE,"E51");var subQ22=sQuery(id+"F0.wireOp",EDGE,"E50");var subQ23=sQuery(id+"F0.wireOp",EDGE,"E49");var subQ24=sQuery(id+"F0.wireOp",EDGE,"E48");var subQ25=sQuery(id+"F0.wireOp",EDGE,"E47.filletArc");var subQ26=sQuery(id+"F0.wireOp",EDGE,"E46.filletArc");var subQ27=sQuery(id+"F0.wireOp",EDGE,"E45.filletArc");var subQ28=sQuery(id+"F0.wireOp",EDGE,"E44.filletArc");var subQ29=sQuery(id+"F0.wireOp",EDGE,"E43");var subQ30=sQuery(id+"F0.wireOp",EDGE,"E42");var subQ31=sQuery(id+"F0.wireOp",EDGE,"E41");var subQ32=sQuery(id+"F0.wireOp",EDGE,"E40");var subQ33=sQuery(id+"F0.wireOp",EDGE,"E39");var subQ34=sQuery(id+"F0.wireOp",EDGE,"E38");var subQ35=sQuery(id+"F0.wireOp",EDGE,"E37");var subQ36=sQuery(id+"F0.wireOp",EDGE,"E36");var subQ37=sQuery(id+"F0.wireOp",EDGE,"E35");var subQ38=sQuery(id+"F0.wireOp",EDGE,"E34");var subQ39=sQuery(id+"F0.wireOp",EDGE,"E33");var subQ40=sQuery(id+"F0.wireOp",EDGE,"E32");var subQ41=sQuery(id+"F0.wireOp",EDGE,"E31");var subQ42=sQuery(id+"F0.wireOp",EDGE,"E30");var subQ43=sQuery(id+"F0.wireOp",EDGE,"E29");var subQ44=sQuery(id+"F0.wireOp",EDGE,"E28");var subQ45=sQuery(id+"F0.wireOp",EDGE,"E27");var subQ46=sQuery(id+"F0.wireOp",EDGE,"E26");var subQ47=sQuery(id+"F0.wireOp",EDGE,"E25");var subQ48=sQuery(id+"F0.wireOp",EDGE,"E24");var subQ49=sQuery(id+"F0.wireOp",EDGE,"E23");var subQ50=sQuery(id+"F0.wireOp",EDGE,"E22");var subQ51=sQuery(id+"F0.wireOp",EDGE,"E21");var subQ52=sQuery(id+"F0.wireOp",EDGE,"E20");var subQ53=sQuery(id+"F0.wireOp",EDGE,"E19");var subQ54=sQuery(id+"F0.wireOp",EDGE,"E18");var subQ55=sQuery(id+"F0.wireOp",EDGE,"E17");var subQ56=sQuery(id+"F0.wireOp",EDGE,"E16");var subQ57=sQuery(id+"F0.wireOp",EDGE,"E15");var subQ58=sQuery(id+"F0.wireOp",EDGE,"E14");var subQ59=sQuery(id+"F0.wireOp",EDGE,"E13");var subQ60=sQuery(id+"F0.wireOp",EDGE,"E12.filletArc");var subQ61=sQuery(id+"F0.wireOp",EDGE,"E11.filletArc");var subQ62=sQuery(id+"F0.wireOp",EDGE,"E10");var subQ63=sQuery(id+"F0.wireOp",EDGE,"E9");var subQ64=sQuery(id+"F0.wireOp",EDGE,"E8");var subQ65=sQuery(id+"F0.wireOp",EDGE,"E7.filletArc");var subQ66=sQuery(id+"F0.wireOp",EDGE,"E6");var subQ67=sQuery(id+"F0.wireOp",EDGE,"E5");var subQ68=sQuery(id+"F0.wireOp",EDGE,"E4");var subQ69=sQuery(id+"F0.wireOp",EDGE,"E3");var subQ70=sQuery(id+"F0.wireOp",EDGE,"E1");var subQ71=sQuery(id+"F0.wireOp",EDGE,"E0");Q0=makeQuery(id+"F2.opShell","OFFSET_FACE",FACE,{"disambiguationData":[OSD([subQ71,subQ70,subQ69,subQ68,subQ67,subQ66,subQ65,subQ64,subQ63,subQ62,subQ61,subQ60,subQ59,subQ58,subQ57,subQ56,subQ55,subQ54,subQ53,subQ52,subQ51,subQ50,subQ49,subQ48,subQ47,subQ46,subQ45,subQ44,subQ43,subQ42,subQ41,subQ40,subQ39,subQ38,subQ37,subQ36,subQ35,subQ34,subQ33,subQ32,subQ31,subQ30,subQ29,subQ28,subQ27,subQ26,subQ25,subQ24,subQ23,subQ22,subQ21,subQ20,subQ19,subQ18,subQ17,subQ16,subQ15,subQ14,subQ13,subQ12,subQ11,subQ10,subQ9,subQ8,subQ7,subQ6,subQ5,subQ4,subQ3,subQ2,subQ1,subQ0]),TDD([makeQuery(id+"F1.opExtrude","CAP_FACE",FACE,{"disambiguationData":[OSD([subQ71,subQ70,subQ69,subQ68,subQ67,subQ66,subQ65,subQ64,subQ63,subQ62,subQ61,subQ60,subQ59,subQ58,subQ57,subQ56,subQ55,subQ54,subQ53,subQ52,subQ51,subQ50,subQ49,subQ48,subQ47,subQ46,subQ45,subQ44,subQ43,subQ42,subQ41,subQ40,subQ39,subQ38,subQ37,subQ36,subQ35,subQ34,subQ33,subQ32,subQ31,subQ30,subQ29,subQ28,subQ27,subQ26,subQ25,subQ24,subQ23,subQ22,subQ21,subQ20,subQ19,subQ18,subQ17,subQ16,subQ15,subQ14,subQ13,subQ12,subQ11,subQ10,subQ9,subQ8,subQ7,subQ6,subQ5,subQ4,subQ3,subQ2,subQ1,subQ0])],"isStart":false})]),OD(1.0)]});}
            extrude(context, id + "F5", {"entities" : qUnion([Q0]), "operationType" : NewBodyOperationType.REMOVE, "oppositeDirection" : true, "depth" : 25 * mm});
        }
        {
            var Q0;
            {var subQ0=sQuery(id+"F0.wireOp",EDGE,"E75");var subQ1=sQuery(id+"F0.wireOp",EDGE,"E73");var subQ2=sQuery(id+"F0.wireOp",EDGE,"E72");var subQ3=sQuery(id+"F0.wireOp",EDGE,"E71");var subQ4=sQuery(id+"F0.wireOp",EDGE,"E70");var subQ5=sQuery(id+"F0.wireOp",EDGE,"E69");var subQ6=sQuery(id+"F0.wireOp",EDGE,"E68");var subQ7=sQuery(id+"F0.wireOp",EDGE,"E67");var subQ8=sQuery(id+"F0.wireOp",EDGE,"E64");var subQ9=sQuery(id+"F0.wireOp",EDGE,"E63.filletArc");var subQ10=sQuery(id+"F0.wireOp",EDGE,"E62.filletArc");var subQ11=sQuery(id+"F0.wireOp",EDGE,"E61");var subQ12=sQuery(id+"F0.wireOp",EDGE,"E60");var subQ13=sQuery(id+"F0.wireOp",EDGE,"E59");var subQ14=sQuery(id+"F0.wireOp",EDGE,"E58.filletArc");var subQ15=sQuery(id+"F0.wireOp",EDGE,"E57.filletArc");var subQ16=sQuery(id+"F0.wireOp",EDGE,"E56.filletArc");var subQ17=sQuery(id+"F0.wireOp",EDGE,"E55.filletArc");var subQ18=sQuery(id+"F0.wireOp",EDGE,"E54");var subQ19=sQuery(id+"F0.wireOp",EDGE,"E53");var subQ20=sQuery(id+"F0.wireOp",EDGE,"E52");var subQ21=sQuery(id+"F0.wireOp",EDGE,"E51");var subQ22=sQuery(id+"F0.wireOp",EDGE,"E50");var subQ23=sQuery(id+"F0.wireOp",EDGE,"E49");var subQ24=sQuery(id+"F0.wireOp",EDGE,"E48");var subQ25=sQuery(id+"F0.wireOp",EDGE,"E47.filletArc");var subQ26=sQuery(id+"F0.wireOp",EDGE,"E46.filletArc");var subQ27=sQuery(id+"F0.wireOp",EDGE,"E45.filletArc");var subQ28=sQuery(id+"F0.wireOp",EDGE,"E44.filletArc");var subQ29=sQuery(id+"F0.wireOp",EDGE,"E43");var subQ30=sQuery(id+"F0.wireOp",EDGE,"E42");var subQ31=sQuery(id+"F0.wireOp",EDGE,"E41");var subQ32=sQuery(id+"F0.wireOp",EDGE,"E40");var subQ33=sQuery(id+"F0.wireOp",EDGE,"E39");var subQ34=sQuery(id+"F0.wireOp",EDGE,"E38");var subQ35=sQuery(id+"F0.wireOp",EDGE,"E37");var subQ36=sQuery(id+"F0.wireOp",EDGE,"E36");var subQ37=sQuery(id+"F0.wireOp",EDGE,"E35");var subQ38=sQuery(id+"F0.wireOp",EDGE,"E34");var subQ39=sQuery(id+"F0.wireOp",EDGE,"E33");var subQ40=sQuery(id+"F0.wireOp",EDGE,"E32");var subQ41=sQuery(id+"F0.wireOp",EDGE,"E31");var subQ42=sQuery(id+"F0.wireOp",EDGE,"E30");var subQ43=sQuery(id+"F0.wireOp",EDGE,"E29");var subQ44=sQuery(id+"F0.wireOp",EDGE,"E28");var subQ45=sQuery(id+"F0.wireOp",EDGE,"E27");var subQ46=sQuery(id+"F0.wireOp",EDGE,"E26");var subQ47=sQuery(id+"F0.wireOp",EDGE,"E25");var subQ48=sQuery(id+"F0.wireOp",EDGE,"E24");var subQ49=sQuery(id+"F0.wireOp",EDGE,"E23");var subQ50=sQuery(id+"F0.wireOp",EDGE,"E22");var subQ51=sQuery(id+"F0.wireOp",EDGE,"E21");var subQ52=sQuery(id+"F0.wireOp",EDGE,"E20");var subQ53=sQuery(id+"F0.wireOp",EDGE,"E19");var subQ54=sQuery(id+"F0.wireOp",EDGE,"E18");var subQ55=sQuery(id+"F0.wireOp",EDGE,"E17");var subQ56=sQuery(id+"F0.wireOp",EDGE,"E16");var subQ57=sQuery(id+"F0.wireOp",EDGE,"E15");var subQ58=sQuery(id+"F0.wireOp",EDGE,"E14");var subQ59=sQuery(id+"F0.wireOp",EDGE,"E13");var subQ60=sQuery(id+"F0.wireOp",EDGE,"E12.filletArc");var subQ61=sQuery(id+"F0.wireOp",EDGE,"E11.filletArc");var subQ62=sQuery(id+"F0.wireOp",EDGE,"E10");var subQ63=sQuery(id+"F0.wireOp",EDGE,"E9");var subQ64=sQuery(id+"F0.wireOp",EDGE,"E8");var subQ65=sQuery(id+"F0.wireOp",EDGE,"E7.filletArc");var subQ66=sQuery(id+"F0.wireOp",EDGE,"E6");var subQ67=sQuery(id+"F0.wireOp",EDGE,"E5");var subQ68=sQuery(id+"F0.wireOp",EDGE,"E4");var subQ69=sQuery(id+"F0.wireOp",EDGE,"E3");var subQ70=sQuery(id+"F0.wireOp",EDGE,"E1");var subQ71=sQuery(id+"F0.wireOp",EDGE,"E0");Q0=makeQuery(id+"F2.opShell","OFFSET_FACE",FACE,{"disambiguationData":[OSD([subQ71,subQ70,subQ69,subQ68,subQ67,subQ66,subQ65,subQ64,subQ63,subQ62,subQ61,subQ60,subQ59,subQ58,subQ57,subQ56,subQ55,subQ54,subQ53,subQ52,subQ51,subQ50,subQ49,subQ48,subQ47,subQ46,subQ45,subQ44,subQ43,subQ42,subQ41,subQ40,subQ39,subQ38,subQ37,subQ36,subQ35,subQ34,subQ33,subQ32,subQ31,subQ30,subQ29,subQ28,subQ27,subQ26,subQ25,subQ24,subQ23,subQ22,subQ21,subQ20,subQ19,subQ18,subQ17,subQ16,subQ15,subQ14,subQ13,subQ12,subQ11,subQ10,subQ9,subQ8,subQ7,subQ6,subQ5,subQ4,subQ3,subQ2,subQ1,subQ0]),TDD([makeQuery(id+"F1.opExtrude","CAP_FACE",FACE,{"disambiguationData":[OSD([subQ71,subQ70,subQ69,subQ68,subQ67,subQ66,subQ65,subQ64,subQ63,subQ62,subQ61,subQ60,subQ59,subQ58,subQ57,subQ56,subQ55,subQ54,subQ53,subQ52,subQ51,subQ50,subQ49,subQ48,subQ47,subQ46,subQ45,subQ44,subQ43,subQ42,subQ41,subQ40,subQ39,subQ38,subQ37,subQ36,subQ35,subQ34,subQ33,subQ32,subQ31,subQ30,subQ29,subQ28,subQ27,subQ26,subQ25,subQ24,subQ23,subQ22,subQ21,subQ20,subQ19,subQ18,subQ17,subQ16,subQ15,subQ14,subQ13,subQ12,subQ11,subQ10,subQ9,subQ8,subQ7,subQ6,subQ5,subQ4,subQ3,subQ2,subQ1,subQ0])],"isStart":false})]),OD(5.0)]});}
            extrude(context, id + "F6", {"entities" : qUnion([Q0]), "operationType" : NewBodyOperationType.REMOVE, "oppositeDirection" : true, "depth" : 25 * mm});
        }
    });
